# Revit family: 4452_Conventional Smoke Detector
name_source: partatom
category: Fire Alarm Devices
units: mm (PartAtom-declared; Revit-internal decimal feet)

## family parameters
Cut with Voids When Loaded = No
Host = Face
Maintain Annotation Orientation = No
OmniClass Number = 23.85.30.21
OmniClass Title = Environmental Detection/Registration
Part Type = Normal
Room Calculation Point = No
Round Connector Dimension = Use Diameter
Shared = No

## types (2) — shared parameters
Ambient Humidity = Maximum 95 % RH
Ambient Temperature Operating = -10 to +50 °C
Ambient Temperature Storage = -25 to +70 °C
CPR = 0786-CPR-21252
Clearance Area = Clearance Area
Current (Active) = Min 3 mA
Current Quiescent = 0.04 mA
H_Base (mm) = 13 mm
H_Detector (mm) = 38 mm  [stored 0.124672 ft]
H_Total (mm) = 51 mm
Ingress Protection Rating = IP41
Manufacturer = Panasonic
Max_Wire Size = Ø 1.6 mm (2 mm²)
Min_Wire Size = Ø 0.6 mm (0.3 mm²)
Omniclass Code = 23.85.30.21.11.11.11
Omniclass Description = Smoke Detectors
Tested and Approved = EN54-7
Type Comments = The photoelectric smoke detector 4452 is a conventional detector. Artificial Intelligence uses smoke sensing for the fire judgement, as well as variable sensitivity and time  delay based on the smoke changes just before the alarm level is reached.
URL = https://www.panasonic-fire-security.com
Uniclass 2015 Code = Pr_75_80_30_27
Uniclass 2015 Description = Fire and smoke detector bases
Uniformat 2010  Code = D7050
Uniformat 2010 Description = Detection and Alarm
Vds Approval = G213028
Version = RVT20
Voltage Allowed = 12 – 30 VDC
Voltage Normal = 24 VDC
Weight = 85g
ø (mm) = 102 mm
zero-valued in all types: Default Elevation

## per-type parameters (varying)
| type | Bases | Description | Model | Product Material |
| 4452_2423 | Base_2324 : 2423 | Conventional photoelectric smoke detector 4452 with 2423 conventional base | 4452 | Polycarbonate_Panasonic_Grey |
| 4452W_2423W | Base_2324 : 2423W | Conventional photoelectric smoke detector 4452W with 2423W conventional base | 4452W | Polycarbonate_Panasonic_White |

note: [stored X ft] marks values corroborated as IEEE doubles in the binary element streams (Revit-internal decimal feet)

## geometry (parser evidence)
native form markers: Blend x36, Sweep x3
no freeform markers — native parametric forms only
